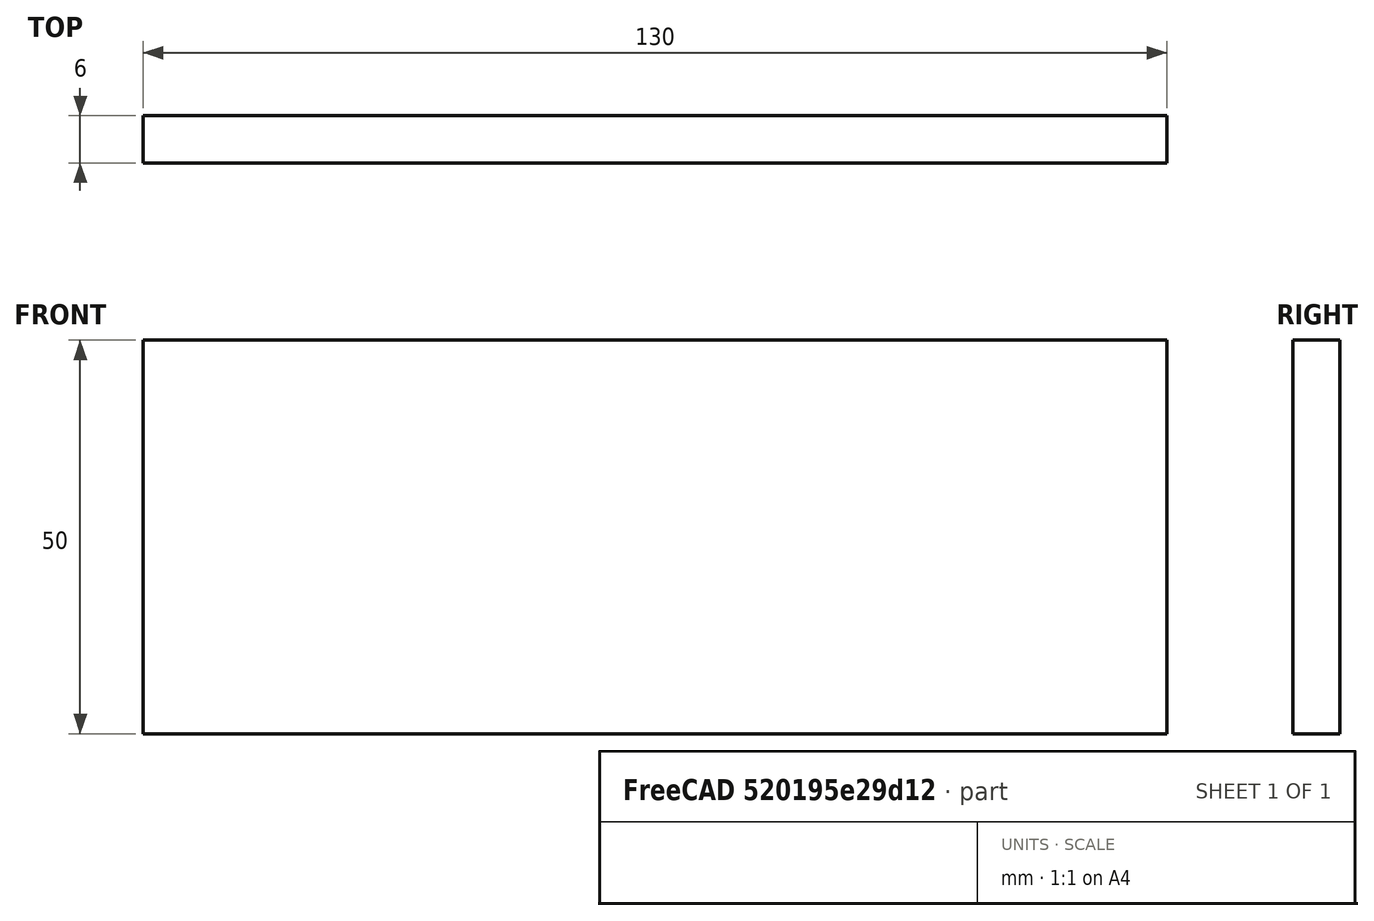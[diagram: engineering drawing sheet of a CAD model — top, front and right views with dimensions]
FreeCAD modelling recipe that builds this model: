
FCSTD DOCUMENT  (FreeCAD 0.15R4671 (Git))
Label: Flat Bar 130x6 EN10058 S235JR
License: All rights reserved
LicenseURL: http://en.wikipedia.org/wiki/All_rights_reserved
objects: Sketcher::SketchObject×1, Part::Extrusion×1
note: 2 computed .brp shape members not serialized (recipe doc carries the construction recipe); baked Part::Feature solids carry a one-line shape summary decoded from their .brp

FEATURE [Sketcher::SketchObject] Sketch
  sketch-geometry (4):
    g0: LineSegment StartX=-65 StartY=-3 StartZ=0 EndX=65 EndY=-3 EndZ=0
    g1: LineSegment StartX=65 StartY=-3 StartZ=0 EndX=65 EndY=3 EndZ=0
    g2: LineSegment StartX=65 StartY=3 StartZ=0 EndX=-65 EndY=3 EndZ=0
    g3: LineSegment StartX=-65 StartY=3 StartZ=0 EndX=-65 EndY=-3 EndZ=0
  constraints (12):
    c: Coincident(g0,g1)
    c: Coincident(g1,g2)
    c: Coincident(g2,g3)
    c: Coincident(g3,g0)
    c: Horizontal(g0)
    c: Horizontal(g2)
    c: Vertical(g1)
    c: Vertical(g3)
    c: Symmetric(g1,g2,g-2)
    c: Symmetric(g0,g1,g-1)
    c: DistanceY(g1) = 6
    c: DistanceX(g0) = 130
FEATURE [Part::Extrusion] Extrude  label="Flat Bar 130x6 EN10058 S235JR"
  Base = -> Sketch
  Dir = (0,0,50)
  Solid = true
